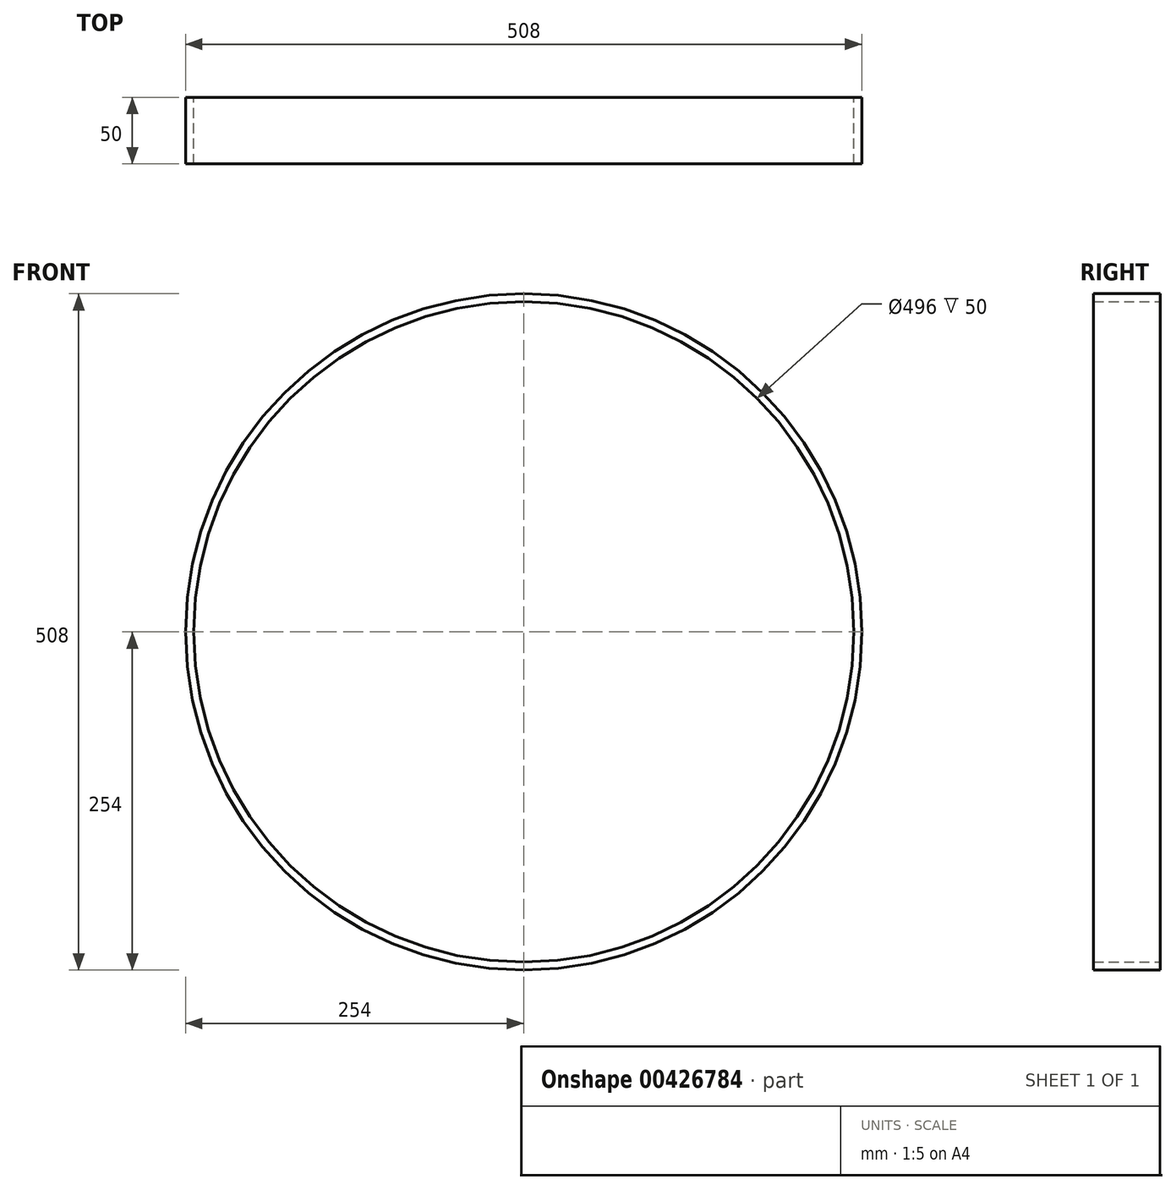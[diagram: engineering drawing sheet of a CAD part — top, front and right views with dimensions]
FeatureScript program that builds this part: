
annotation { "Feature Type Name" : "Feature", "Feature Type Description" : "" }
export const myFeature = defineFeature(function(context is Context, id is Id, definition is map)
    precondition{}
    {
        {
            var Q0;
            Q0=qCreatedBy(makeId("Front.planeOp"),FACE);
            var sketch = newSketch(context, id + "F0", { "sketchPlane" : qUnion([Q0])});
            skCircle(sketch, "E0", {"center": v(0, 0) * mm, "radius": 254 * mm});
            skCircle(sketch, "E1.0", {"center": v(0, 0) * mm, "radius": 248 * mm});
            skSolve(sketch);
        }
        {
            var Q0;
            Q0=makeQuery(id+"F0.imprint","IMPRINT",FACE,{"disambiguationData":[TD([[makeQuery(id+"F0.imprint","IMPRINT",EDGE,{"derivedFrom":sQuery(id+"F0.wireOp",EDGE,"E0")}),1.0]])]});
            extrude(context, id + "F1", {"entities" : qUnion([Q0]), "depth" : 50 * mm});
        }
    });
